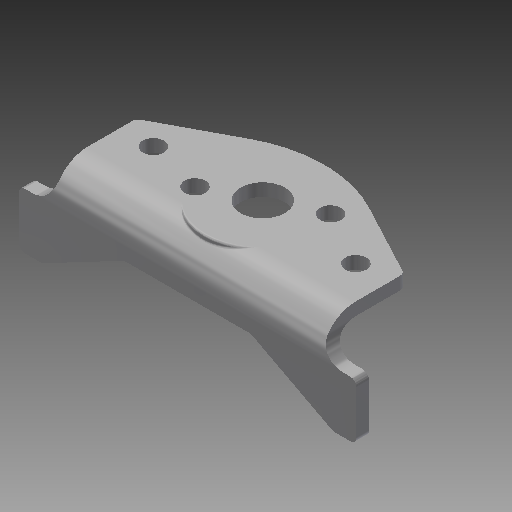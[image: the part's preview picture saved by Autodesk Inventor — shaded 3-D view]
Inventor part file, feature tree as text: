
AUTODESK INVENTOR PART (.ipt)
format: ipt  version: 2019 (Build 230136000, 136)  size: 268,800 bytes
history: native  units: mm
features: fillet x7, extrude x5, sketch x5, hole x1
ambient origin geometry x8: Origin, YZ Plane, XZ Plane, XY Plane, X Axis, Y Axis, Z Axis, Center Point
bodies: Solid1 (feature_tree)
feature tree (18):
  extrude  "Extrusion1"  Depth=8.0mm
  extrude  "Extrusion2"  Depth=8.25mm
  fillet  "Fillet1"  Radius=21.25mm
  fillet  "Fillet2"  Radius=30.0mm
  fillet  "Fillet3"  Radius=15.0mm
  fillet  "Fillet4"  Radius=11.0mm
  extrude  "Extrusion3"  Depth=5.5mm
  extrude  "Extrusion4"  Depth=3.0mm
  fillet  "Fillet5"  Radius=19.5mm
  fillet  "Fillet6"  Radius=10.821041mm
  sketch  "Sketch5"  dims[d15=10.821041mm d16=30.0mm d17=3.0mm d18=0.0mm d19=5.0mm d20=8.0mm d21=5.0mm d22=1.5mm d23=9.8mm d24=28.0mm d25=2.0mm d26=0.0mm d27=4.0mm d28=0.0mm d29=0.5mm d30=0.5mm d31=1.0mm d32=10.5mm d33=10.8mm d34=24.0mm d35=10.8mm d36=24.0mm d37=1.935232mm d38=5.25mm d39=5.25mm d40=1.934704mm d41=2.0mm d42=0.0mm d43=5.0mm d44=6.0mm d45=4.0mm d46=2.0mm d47=90.0deg d48=8.0mm d49=20.594885mm d50=1.5mm d51=31.75mm]
  extrude  "Extrusion5"  Depth=31.75mm
  hole  "Hole1"  [1 undecoded]
  fillet  "Fillet7"  Radius=5.0mm
  sketch  "Sketch1"  dims[d0=63.5mm d1=8.0mm]
  sketch  "Sketch2"  dims[d2=8.25mm d3=8.25mm d4=21.25mm d5=30.0mm d6=15.0mm d7=11.0mm]
  sketch  "Sketch3"  dims[d8=5.5mm d9=5.5mm]
  sketch  "Sketch4"  dims[d10=3.0mm d11=0.0mm d12=19.5mm d13=19.5mm d14=10.821041mm]
note: 1 required parameter value undecoded (feature->parameter linkage not recoverable at this tier; creation-order binding heuristic only, values carry confidence <= 0.55)
